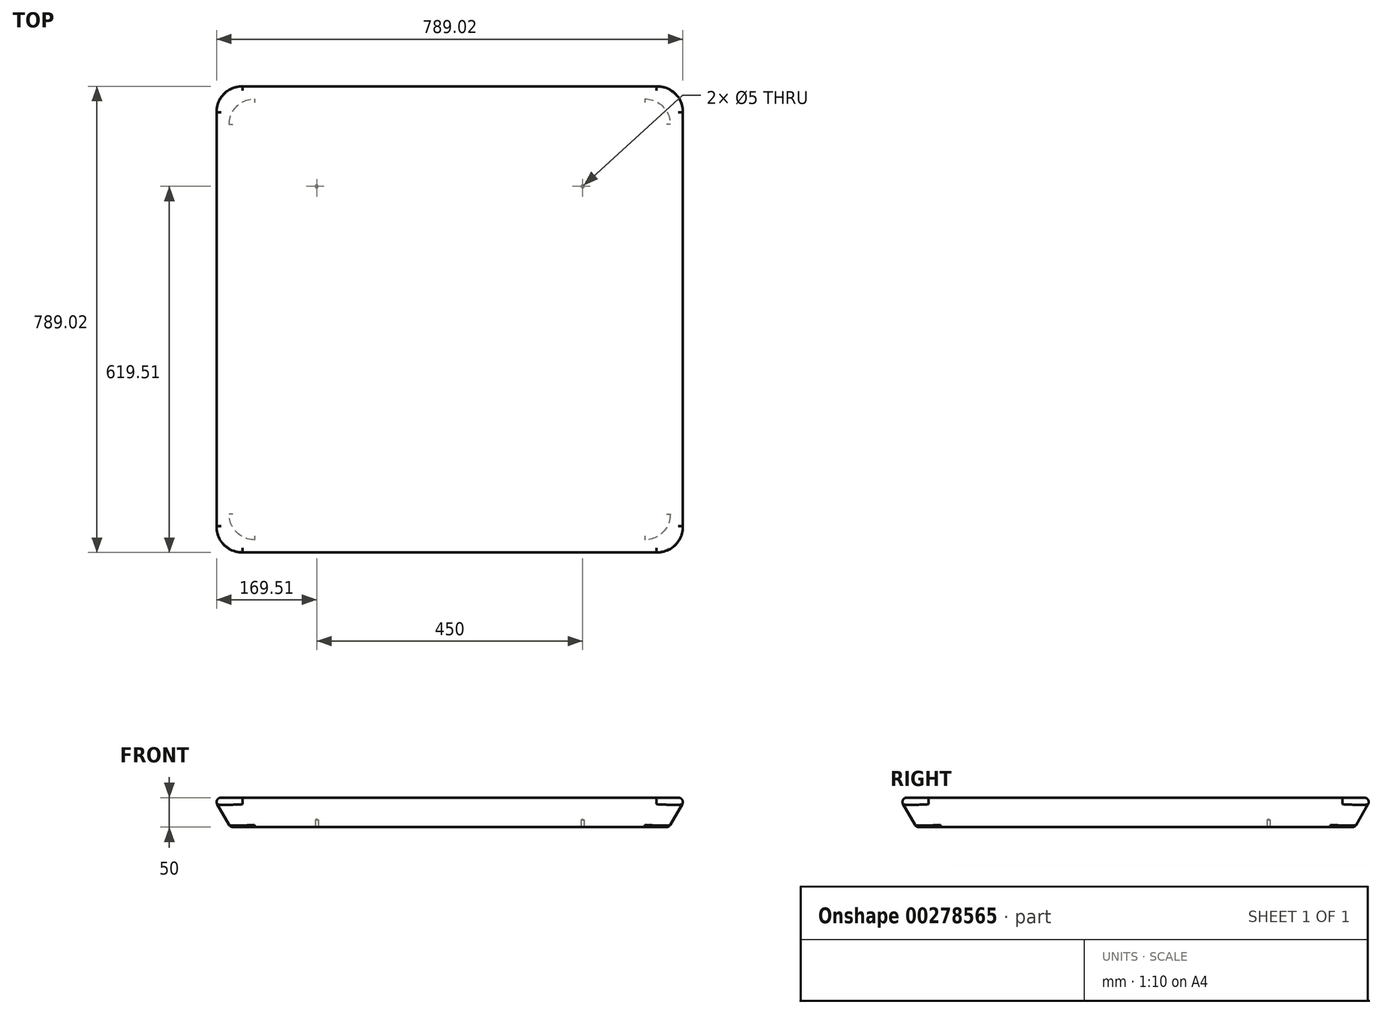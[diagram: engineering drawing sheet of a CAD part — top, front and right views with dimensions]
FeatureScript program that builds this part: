
annotation { "Feature Type Name" : "Feature", "Feature Type Description" : "" }
export const myFeature = defineFeature(function(context is Context, id is Id, definition is map)
    precondition{}
    {
        {
            var Q0;
            Q0=qCreatedBy(makeId("Top.planeOp"),FACE);
            var sketch = newSketch(context, id + "F0", { "sketchPlane" : qUnion([Q0])});
            skLineSegment(sketch, "E0.bottom", {"start": v(-400, 400) * mm, "end": v(400, 400) * mm});
            skLineSegment(sketch, "E0.top", {"start": v(-400, -400) * mm, "end": v(400, -400) * mm});
            skLineSegment(sketch, "E0.left", {"start": v(-400, 400) * mm, "end": v(-400, -400) * mm});
            skLineSegment(sketch, "E0.right", {"start": v(400, 400) * mm, "end": v(400, -400) * mm});
            skLineSegment(sketch, "E1", {"start": v(-303.37, 0) * mm, "end": v(434.83, 0) * mm, "construction": true});
            skLineSegment(sketch, "E2", {"start": v(0, 384.27) * mm, "end": v(0, -415.73) * mm, "construction": true});
            skSolve(sketch);
        }
        {
            var Q0;
            Q0=makeQuery(id+"F0.imprint","IMPRINT",FACE,{"disambiguationData":[TD([[makeQuery(id+"F0.imprint","IMPRINT",EDGE,{"derivedFrom":sQuery(id+"F0.wireOp",EDGE,"E0.bottom")}),-1.0]])]});
            extrude(context, id + "F3", {"entities" : qUnion([Q0]), "oppositeDirection" : true, "depth" : 50 * mm, "hasDraft" : true, "draftAngle" : 30 * degree, "draftPullDirection" : true});
        }
        {
            var Q0;
            Q0=makeQuery(id+"F3.opExtrude","SWEPT_EDGE",EDGE,{"disambiguationData":[OSD([sQuery(id+"F0.wireOp",EDGE,"E0.top"),sQuery(id+"F0.wireOp",EDGE,"E0.left")])]});
            var Q1;
            Q1=makeQuery(id+"F3.opExtrude","SWEPT_EDGE",EDGE,{"disambiguationData":[OSD([sQuery(id+"F0.wireOp",EDGE,"E0.top"),sQuery(id+"F0.wireOp",EDGE,"E0.right")])]});
            var Q2;
            Q2=makeQuery(id+"F3.opExtrude","SWEPT_EDGE",EDGE,{"disambiguationData":[OSD([sQuery(id+"F0.wireOp",EDGE,"E0.bottom"),sQuery(id+"F0.wireOp",EDGE,"E0.right")])]});
            var Q3;
            Q3=makeQuery(id+"F3.opExtrude","SWEPT_EDGE",EDGE,{"disambiguationData":[OSD([sQuery(id+"F0.wireOp",EDGE,"E0.bottom"),sQuery(id+"F0.wireOp",EDGE,"E0.left")])]});
            fillet(context, id + "F4", {"entities" : qUnion([Q0, Q1, Q2, Q3]), "radius" : 50 * mm, "tangentPropagation" : true, "allowEdgeOverflow" : false});
        }
        {
            var Q0;
            Q0=makeQuery(id+"F3.opExtrude","CAP_FACE",FACE,{"disambiguationData":[OSD([sQuery(id+"F0.wireOp",EDGE,"E0.bottom"),sQuery(id+"F0.wireOp",EDGE,"E0.top"),sQuery(id+"F0.wireOp",EDGE,"E0.left"),sQuery(id+"F0.wireOp",EDGE,"E0.right")])],"isStart":true});
            var Q1;
            Q1=makeQuery(id+"F3.opExtrude","CAP_FACE",FACE,{"disambiguationData":[OSD([sQuery(id+"F0.wireOp",EDGE,"E0.bottom"),sQuery(id+"F0.wireOp",EDGE,"E0.top"),sQuery(id+"F0.wireOp",EDGE,"E0.left"),sQuery(id+"F0.wireOp",EDGE,"E0.right")])],"isStart":false});
            fillet(context, id + "F1", {"entities" : qUnion([Q0, Q1]), "radius" : 7.5 * mm, "tangentPropagation" : true, "allowEdgeOverflow" : false});
        }
        {
            var Q0;
            Q0=makeQuery(id+"F3.opExtrude","CAP_FACE",FACE,{"disambiguationData":[OSD([sQuery(id+"F0.wireOp",EDGE,"E0.bottom"),sQuery(id+"F0.wireOp",EDGE,"E0.top"),sQuery(id+"F0.wireOp",EDGE,"E0.left"),sQuery(id+"F0.wireOp",EDGE,"E0.right")])],"isStart":false});
            var sketch = newSketch(context, id + "F5", { "sketchPlane" : qUnion([Q0])});
            skLineSegment(sketch, "E3.0", {"start": v(330, 366.8) * mm, "end": v(-330, 366.8) * mm, "construction": true});
            skLineSegment(sketch, "E4.bottom", {"start": v(-225, 225) * mm, "end": v(225, 225) * mm, "construction": true});
            skLineSegment(sketch, "E4.top", {"start": v(-225, -225) * mm, "end": v(225, -225) * mm, "construction": true});
            skLineSegment(sketch, "E4.left", {"start": v(-225, 225) * mm, "end": v(-225, -225) * mm, "construction": true});
            skLineSegment(sketch, "E4.right", {"start": v(225, 225) * mm, "end": v(225, -225) * mm, "construction": true});
            skLineSegment(sketch, "E5", {"start": v(168.75, 0) * mm, "end": v(-225, 0) * mm, "construction": true});
            skLineSegment(sketch, "E6", {"start": v(0, 77.58) * mm, "end": v(0, -139.93) * mm, "construction": true});
            skCircle(sketch, "E7", {"center": v(-225, 225) * mm, "radius": 10 * mm});
            skCircle(sketch, "E8.0.1.0", {"center": v(-225, -225) * mm, "radius": 10 * mm});
            skCircle(sketch, "E8.1.0.0", {"center": v(225, 225) * mm, "radius": 10 * mm});
            skCircle(sketch, "E8.1.1.0", {"center": v(225, -225) * mm, "radius": 10 * mm});
            skSolve(sketch);
        }
        {
            var Q0;
            Q0=sQuery(id+"F5.wireOp",VERTEX,"E4.bottom.end");
            var Q1;
            Q1=sQuery(id+"F5.wireOp",VERTEX,"E4.left.start");
            var Q2;
            Q2=sQuery(id+"F5.wireOp",VERTEX,"E4.top.start");
            var Q3;
            Q3=sQuery(id+"F5.wireOp",VERTEX,"E4.right.end");
            var Q4;
            Q4=makeQuery(id+"F3.opExtrude","SWEPT_BODY",BODY,{"disambiguationData":[OSD([sQuery(id+"F0.wireOp",EDGE,"E0.bottom"),sQuery(id+"F0.wireOp",EDGE,"E0.top"),sQuery(id+"F0.wireOp",EDGE,"E0.left"),sQuery(id+"F0.wireOp",EDGE,"E0.right")])]});
            hole(context, id + "F2", {"style" : HoleStyle.SIMPLE, "endStyle" : HoleEndStyle.BLIND, "holeDiameter" : 5 * mm, "holeDepth" : 12 * mm, "tappedDepth" : 12 * mm, "tapClearance" : 3, "locations" : qUnion([Q0, Q1, Q2, Q3]), "scope" : qUnion([Q4])});
        }
    });
